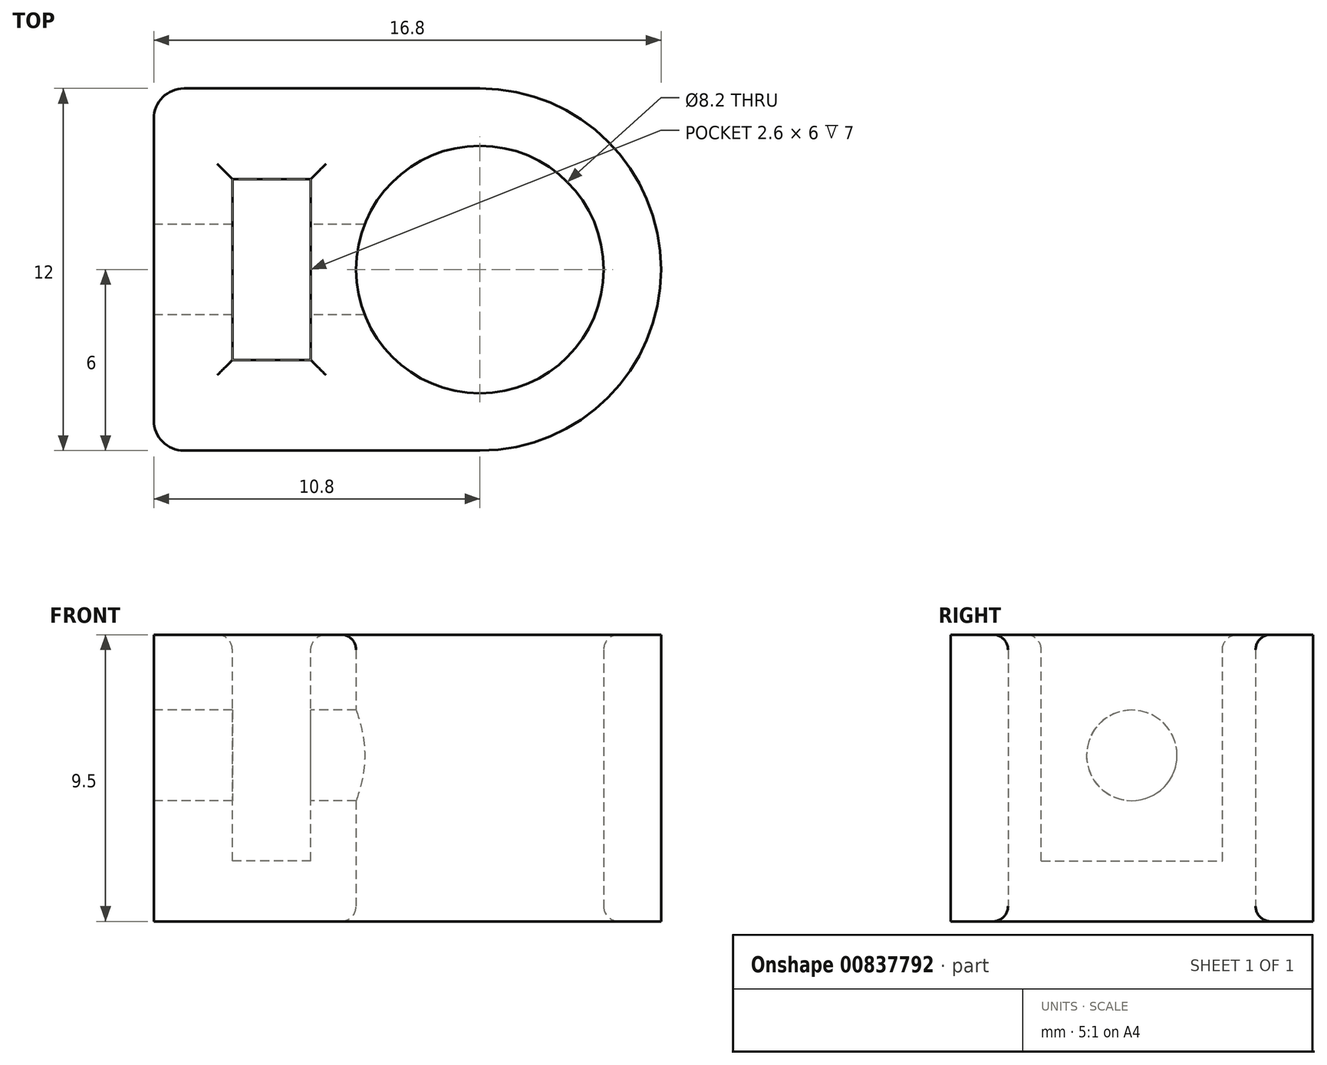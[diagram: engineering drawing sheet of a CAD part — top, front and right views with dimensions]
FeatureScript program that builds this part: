
annotation { "Feature Type Name" : "Feature", "Feature Type Description" : "" }
export const myFeature = defineFeature(function(context is Context, id is Id, definition is map)
    precondition{}
    {
        {
            var Q0;
            Q0=qCreatedBy(makeId("Top.planeOp"),FACE);
            var sketch = newSketch(context, id + "F0", { "sketchPlane" : qUnion([Q0])});
            skCircle(sketch, "E0", {"center": v(0, 0) * mm, "radius": 6 * mm});
            skCircle(sketch, "E1", {"center": v(0, 0) * mm, "radius": 4.1 * mm});
            skLineSegment(sketch, "E2", {"start": v(0, 6) * mm, "end": v(-6, 6) * mm});
            skLineSegment(sketch, "E3", {"start": v(-6, 0) * mm, "end": v(-6, 6) * mm});
            skLineSegment(sketch, "E4", {"start": v(0, -6) * mm, "end": v(-6, -6) * mm});
            skLineSegment(sketch, "E5", {"start": v(-6, 6) * mm, "end": v(-6, -6) * mm});
            skLineSegment(sketch, "E6", {"start": v(-6, 6) * mm, "end": v(-10.8, 6) * mm});
            skLineSegment(sketch, "E7", {"start": v(-4.1, 0) * mm, "end": v(-5.6, 0) * mm, "construction": true});
            skLineSegment(sketch, "E8", {"start": v(-5.6, 0) * mm, "end": v(-8.2, 0) * mm});
            skLineSegment(sketch, "E9", {"start": v(-6, -6) * mm, "end": v(-10.8, -6) * mm});
            skLineSegment(sketch, "E10", {"start": v(-10.8, -6) * mm, "end": v(-10.8, 6) * mm});
            skSolve(sketch);
        }
        {
            var Q0;
            Q0=makeQuery(id+"F0.imprint","IMPRINT",FACE,{"disambiguationData":[TD([[makeQuery(id+"F0.imprint","IMPRINT",EDGE,{"derivedFrom":sQuery(id+"F0.wireOp",EDGE,"E1")}),-1.0]])]});
            extrude(context, id + "F1", {"entities" : qUnion([Q0]), "depth" : 12 * mm, "offsetDistance" : 25 * mm});
        }
        {
            var Q0;
            {var subQ0=sQuery(id+"F0.wireOp",EDGE,"E2");Q0=makeQuery(id+"F0.imprint","IMPRINT",FACE,{"disambiguationData":[TD([[makeQuery(id+"F0.imprint","IMPRINT",EDGE,{"derivedFrom":subQ0}),1.0]])]});}
            var Q1;
            {var subQ2=sQuery(id+"F0.wireOp",EDGE,"E4");Q1=makeQuery(id+"F0.imprint","IMPRINT",FACE,{"disambiguationData":[TD([[makeQuery(id+"F0.imprint","IMPRINT",EDGE,{"derivedFrom":subQ2}),-1.0]])]});}
            var Q2;
            Q2=makeQuery(id+"F0.imprint","IMPRINT",FACE,{"disambiguationData":[TD([[makeQuery(id+"F0.imprint","IMPRINT",EDGE,{"derivedFrom":sQuery(id+"F0.wireOp",EDGE,"E3")}),1.0]])]});
            extrude(context, id + "F2", {"entities" : qUnion([Q0, Q1, Q2]), "operationType" : NewBodyOperationType.ADD, "depth" : 12 * mm, "offsetDistance" : 25 * mm});
        }
        {
            var Q0;
            {var subQ0=sQuery(id+"F0.wireOp",EDGE,"E0");Q0=makeQuery(id+"F2.boolean.opBoolean","MERGE",FACE,{"derivedFrom":[makeQuery(id+"F1.opExtrude","CAP_FACE",FACE,{"disambiguationData":[OSD([subQ0,sQuery(id+"F0.wireOp",EDGE,"E1")])],"isStart":false}),makeQuery(id+"F2.opExtrude","CAP_FACE",FACE,{"disambiguationData":[OSD([subQ0,sQuery(id+"F0.wireOp",EDGE,"E2"),sQuery(id+"F0.wireOp",EDGE,"E4"),sQuery(id+"F0.wireOp",EDGE,"E6"),sQuery(id+"F0.wireOp",EDGE,"E9"),sQuery(id+"F0.wireOp",EDGE,"E10")])],"isStart":false})]});}
            var sketch = newSketch(context, id + "F3", { "sketchPlane" : qUnion([Q0])});
            skLineSegment(sketch, "E11", {"start": v(-6, 0) * mm, "end": v(-4.1, 0) * mm, "construction": true});
            skLineSegment(sketch, "E12", {"start": v(-4.1, 0) * mm, "end": v(-5.6, 0) * mm, "construction": true});
            skLineSegment(sketch, "E13", {"start": v(-5.6, 0) * mm, "end": v(-5.6, 3) * mm, "construction": true});
            skLineSegment(sketch, "E14", {"start": v(-5.6, 3) * mm, "end": v(-8.2, 3) * mm, "construction": true});
            skLineSegment(sketch, "E15", {"start": v(-8.2, 3) * mm, "end": v(-8.2, -3) * mm, "construction": true});
            skLineSegment(sketch, "E16", {"start": v(-8.2, -3) * mm, "end": v(-5.6, -3) * mm, "construction": true});
            skLineSegment(sketch, "E17", {"start": v(-5.6, -3) * mm, "end": v(-5.6, 0) * mm, "construction": true});
            skLineSegment(sketch, "E18", {"start": v(-5.6, 0) * mm, "end": v(-5.6, 3) * mm});
            skLineSegment(sketch, "E19", {"start": v(-8.2, 3) * mm, "end": v(-8.2, -3) * mm});
            skLineSegment(sketch, "E20", {"start": v(-5.6, -3) * mm, "end": v(-8.2, -3) * mm});
            skLineSegment(sketch, "E21", {"start": v(-5.6, -3) * mm, "end": v(-5.6, 3) * mm});
            skLineSegment(sketch, "E22", {"start": v(-5.6, 3) * mm, "end": v(-8.2, 3) * mm});
            skLineSegment(sketch, "E23", {"start": v(-8.2, 0) * mm, "end": v(-10.8, 0) * mm, "construction": true});
            skLineSegment(sketch, "E24", {"start": v(-5.6, 3) * mm, "end": v(-5.2, 3) * mm});
            skLineSegment(sketch, "E25", {"start": v(-5.6, -3) * mm, "end": v(-5.2, -3) * mm});
            skSolve(sketch);
        }
        {
            var Q0;
            Q0=makeQuery(id+"F3.imprint","IMPRINT",FACE,{"disambiguationData":[TD([[makeQuery(id+"F3.imprint","IMPRINT",EDGE,{"derivedFrom":sQuery(id+"F3.wireOp",EDGE,"E18")}),1.0]])]});
            extrude(context, id + "F4", {"entities" : qUnion([Q0]), "operationType" : NewBodyOperationType.REMOVE, "depth" : 3 * mm, "offsetDistance" : 25 * mm});
        }
        {
            var Q0;
            Q0=makeQuery(id+"F2.opExtrude","SWEPT_FACE",FACE,{"disambiguationData":[OSD([sQuery(id+"F0.wireOp",EDGE,"E10")])]});
            var sketch = newSketch(context, id + "F5", { "sketchPlane" : qUnion([Q0])});
            skLineSegment(sketch, "E26", {"start": v(0, 0) * mm, "end": v(0, 6) * mm});
            skPoint(sketch, "E26.endSnap0", {"position": v(6, 6) * mm});
            skCircle(sketch, "E27", {"center": v(0, 6) * mm, "radius": 1.5 * mm});
            skSolve(sketch);
        }
        {
            var Q0;
            Q0 = qSketchRegion(id + "F5", true);
            extrude(context, id + "F6", {"entities" : qUnion([Q0]), "operationType" : NewBodyOperationType.REMOVE, "oppositeDirection" : true, "depth" : 8 * mm, "offsetDistance" : 25 * mm});
        }
        {
            var Q0;
            Q0=makeQuery(id+"F3.imprint","IMPRINT",FACE,{"disambiguationData":[TD([[makeQuery(id+"F3.imprint","IMPRINT",EDGE,{"derivedFrom":sQuery(id+"F3.wireOp",EDGE,"E18")}),1.0]])]});
            var Q1;
            Q1=makeQuery(id+"F3.imprint","IMPRINT",FACE,{"disambiguationData":[TD([[makeQuery(id+"F3.imprint","IMPRINT",EDGE,{"derivedFrom":sQuery(id+"F3.wireOp",EDGE,"E18")}),1.0]])]});
            extrude(context, id + "F7", {"entities" : qUnion([Q0, Q1]), "operationType" : NewBodyOperationType.REMOVE, "oppositeDirection" : true, "depth" : 9.5 * mm, "offsetDistance" : 25 * mm});
        }
        {
            var Q0;
            Q0=makeQuery(id+"F2.opExtrude","SWEPT_FACE",FACE,{"disambiguationData":[OSD([sQuery(id+"F0.wireOp",EDGE,"E10")])]});
            var sketch = newSketch(context, id + "F8", { "sketchPlane" : qUnion([Q0])});
            skLineSegment(sketch, "E28", {"start": v(6, 12) * mm, "end": v(6, 10) * mm});
            skLineSegment(sketch, "E29", {"start": v(6, 10) * mm, "end": v(-6, 10) * mm});
            skLineSegment(sketch, "E30", {"start": v(-6, 0) * mm, "end": v(-6, 0.5) * mm});
            skLineSegment(sketch, "E31", {"start": v(-6, 0.5) * mm, "end": v(6, 0.5) * mm});
            skSolve(sketch);
        }
        {
            var Q0;
            Q0=makeQuery(id+"F8.imprint","IMPRINT",FACE,{"disambiguationData":[TD([[makeQuery(id+"F8.imprint","IMPRINT",EDGE,{"derivedFrom":sQuery(id+"F8.wireOp",EDGE,"E28")}),-1.0]])]});
            var Q1;
            Q1=makeQuery(id+"F8.imprint","IMPRINT",FACE,{"disambiguationData":[TD([[makeQuery(id+"F8.imprint","IMPRINT",EDGE,{"derivedFrom":sQuery(id+"F8.wireOp",EDGE,"E30")}),1.0]])]});
            extrude(context, id + "F9", {"entities" : qUnion([Q0, Q1]), "operationType" : NewBodyOperationType.REMOVE, "oppositeDirection" : true, "depth" : 25 * mm, "offsetDistance" : 25 * mm});
        }
        {
            var Q0;
            Q0=makeQuery(id+"F9.boolean.opBoolean","COPY",EDGE,{"derivedFrom":makeQuery(id+"F9.opExtrude","SWEPT_EDGE",EDGE,{"disambiguationData":[OSD([sQuery(id+"F0.wireOp",EDGE,"E6"),sQuery(id+"F0.wireOp",EDGE,"E10"),sQuery(id+"F8.wireOp",EDGE,"E29")])]})});
            var Q1;
            Q1=makeQuery(id+"F9.boolean.opBoolean","COPY",EDGE,{"derivedFrom":makeQuery(id+"F9.opExtrude","CAP_EDGE",EDGE,{"disambiguationData":[OSD([sQuery(id+"F8.wireOp",EDGE,"E29")])],"isStart":true})});
            var Q2;
            Q2=makeQuery(id+"F2.opExtrude","SWEPT_EDGE",EDGE,{"disambiguationData":[OSD([sQuery(id+"F0.wireOp",EDGE,"E6"),sQuery(id+"F0.wireOp",EDGE,"E10")])]});
            var Q3;
            Q3=makeQuery(id+"F2.opExtrude","SWEPT_EDGE",EDGE,{"disambiguationData":[OSD([sQuery(id+"F0.wireOp",EDGE,"E9"),sQuery(id+"F0.wireOp",EDGE,"E10")])]});
            fillet(context, id + "F10", {"entities" : qUnion([Q0, Q1, Q2, Q3]), "radius" : 1 * mm, "tangentPropagation" : true, "allowEdgeOverflow" : false});
        }
        {
            var Q0;
            Q0=makeQuery(id+"F6.boolean.opBoolean","COPY",EDGE,{"derivedFrom":makeQuery(id+"F6.opExtrude","CAP_EDGE",EDGE,{"disambiguationData":[OSD([sQuery(id+"F5.wireOp",EDGE,"E27")])],"isStart":true})});
            var Q1;
            Q1=makeQuery(id+"F9.boolean.opBoolean","INTERSECT",EDGE,{"derivedFrom":[makeQuery(id+"F7.boolean.opBoolean","COPY",FACE,{"derivedFrom":makeQuery(id+"F7.opExtrude","SWEPT_FACE",FACE,{"disambiguationData":[OSD([sQuery(id+"F3.wireOp",EDGE,"E19")])]})}),makeQuery(id+"F9.opExtrude","SWEPT_FACE",FACE,{"disambiguationData":[OSD([sQuery(id+"F8.wireOp",EDGE,"E29")])]})]});
            var Q2;
            Q2=makeQuery(id+"F9.boolean.opBoolean","INTERSECT",EDGE,{"derivedFrom":[makeQuery(id+"F7.boolean.opBoolean","COPY",FACE,{"derivedFrom":makeQuery(id+"F7.opExtrude","SWEPT_FACE",FACE,{"disambiguationData":[OSD([sQuery(id+"F3.wireOp",EDGE,"E22")])]})}),makeQuery(id+"F9.opExtrude","SWEPT_FACE",FACE,{"disambiguationData":[OSD([sQuery(id+"F8.wireOp",EDGE,"E29")])]})]});
            var Q3;
            Q3=makeQuery(id+"F9.boolean.opBoolean","INTERSECT",EDGE,{"derivedFrom":[makeQuery(id+"F7.boolean.opBoolean","COPY",FACE,{"derivedFrom":makeQuery(id+"F7.opExtrude","SWEPT_FACE",FACE,{"disambiguationData":[OSD([sQuery(id+"F3.wireOp",EDGE,"E18"),sQuery(id+"F3.wireOp",EDGE,"E21")])]})}),makeQuery(id+"F9.opExtrude","SWEPT_FACE",FACE,{"disambiguationData":[OSD([sQuery(id+"F8.wireOp",EDGE,"E29")])]})]});
            var Q4;
            Q4=makeQuery(id+"F9.boolean.opBoolean","INTERSECT",EDGE,{"derivedFrom":[makeQuery(id+"F7.boolean.opBoolean","COPY",FACE,{"derivedFrom":makeQuery(id+"F7.opExtrude","SWEPT_FACE",FACE,{"disambiguationData":[OSD([sQuery(id+"F3.wireOp",EDGE,"E20")])]})}),makeQuery(id+"F9.opExtrude","SWEPT_FACE",FACE,{"disambiguationData":[OSD([sQuery(id+"F8.wireOp",EDGE,"E29")])]})]});
            var Q5;
            Q5=makeQuery(id+"F9.boolean.opBoolean","INTERSECT",EDGE,{"derivedFrom":[makeQuery(id+"F1.opExtrude","SWEPT_FACE",FACE,{"disambiguationData":[OSD([sQuery(id+"F0.wireOp",EDGE,"E1")])]}),makeQuery(id+"F9.opExtrude","SWEPT_FACE",FACE,{"disambiguationData":[OSD([sQuery(id+"F8.wireOp",EDGE,"E29")])]})]});
            var Q6;
            Q6=makeQuery(id+"F9.boolean.opBoolean","INTERSECT",EDGE,{"derivedFrom":[makeQuery(id+"F1.opExtrude","SWEPT_FACE",FACE,{"disambiguationData":[OSD([sQuery(id+"F0.wireOp",EDGE,"E1")])]}),makeQuery(id+"F9.opExtrude","SWEPT_FACE",FACE,{"disambiguationData":[OSD([sQuery(id+"F8.wireOp",EDGE,"E31")])]})]});
            fillet(context, id + "F11", {"entities" : qUnion([Q0, Q1, Q2, Q3, Q4, Q5, Q6]), "radius" : .5 * mm, "tangentPropagation" : true, "allowEdgeOverflow" : false});
        }
        {
            var Q0;
            Q0=makeQuery(id+"F9.boolean.opBoolean","COPY",FACE,{"derivedFrom":makeQuery(id+"F9.opExtrude","SWEPT_FACE",FACE,{"disambiguationData":[OSD([sQuery(id+"F8.wireOp",EDGE,"E31")])]})});
            var sketch = newSketch(context, id + "F12", { "sketchPlane" : qUnion([Q0])});
            skCircle(sketch, "E32", {"center": v(0, 0) * mm, "radius": 4.1 * mm});
            skSolve(sketch);
        }
        {
            var Q0;
            Q0 = qSketchRegion(id + "F12", true);
            extrude(context, id + "F13", {"entities" : qUnion([Q0]), "operationType" : NewBodyOperationType.ADD, "oppositeDirection" : true, "depth" : 25 * mm, "offsetDistance" : 25 * mm});
        }
        {
            var Q0;
            Q0=makeQuery(id+"F13.opExtrude","CAP_FACE",FACE,{"disambiguationData":[OSD([sQuery(id+"F12.wireOp",EDGE,"E32")])],"isStart":true});
            extrude(context, id + "F14", {"entities" : qUnion([Q0]), "operationType" : NewBodyOperationType.REMOVE, "oppositeDirection" : true, "depth" : 25 * mm, "offsetDistance" : 25 * mm});
        }
    });
